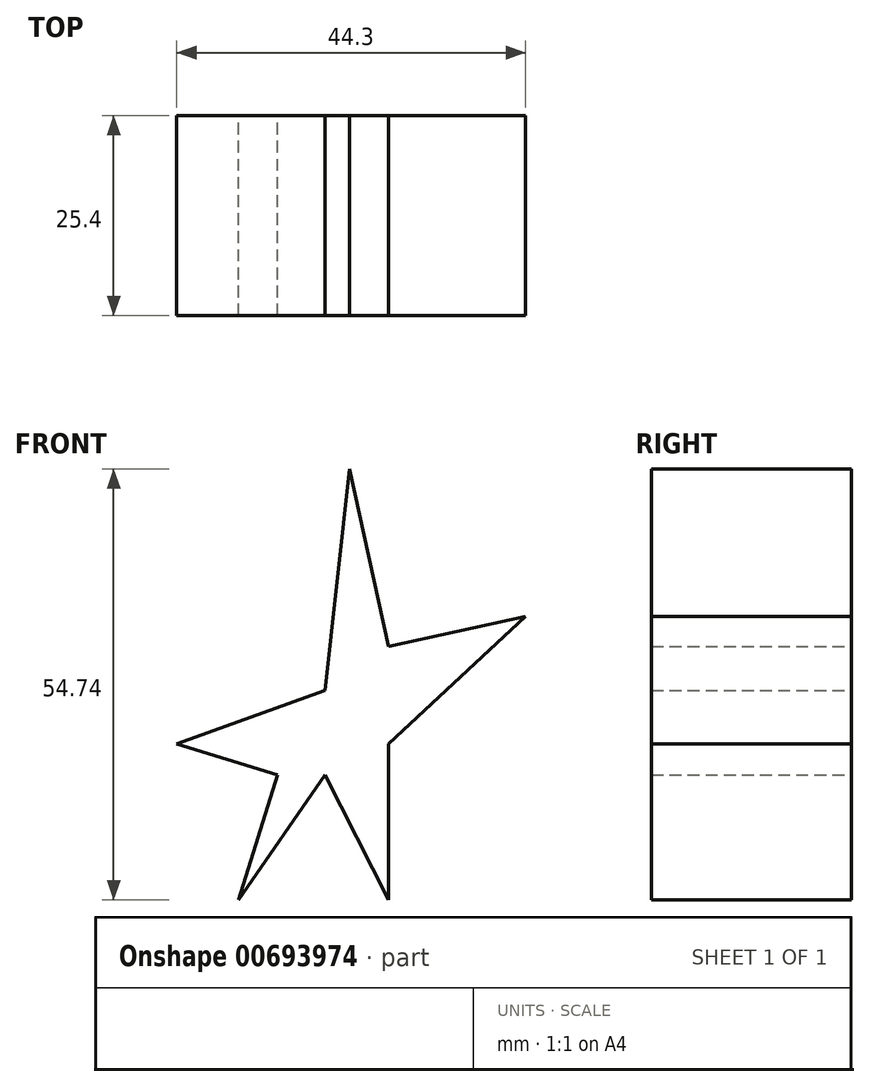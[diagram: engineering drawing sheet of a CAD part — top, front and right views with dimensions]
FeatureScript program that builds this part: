
annotation { "Feature Type Name" : "Feature", "Feature Type Description" : "" }
export const myFeature = defineFeature(function(context is Context, id is Id, definition is map)
    precondition{}
    {
        {
            var Q0;
            Q0=qCreatedBy(makeId("Front.planeOp"),FACE);
            var sketch = newSketch(context, id + "F0", { "sketchPlane" : qUnion([Q0])});
            skLineSegment(sketch, "E0", {"start": v(0, 0) * mm, "end": v(3.11, 28.11) * mm});
            skLineSegment(sketch, "E1", {"start": v(3.11, 28.11) * mm, "end": v(8.03, 5.6) * mm});
            skLineSegment(sketch, "E2", {"start": v(8.03, 5.6) * mm, "end": v(25.46, 9.4) * mm});
            skLineSegment(sketch, "E3", {"start": v(25.46, 9.4) * mm, "end": v(8.03, -6.81) * mm});
            skLineSegment(sketch, "E4", {"start": v(8.03, -6.81) * mm, "end": v(8.03, -26.63) * mm});
            skLineSegment(sketch, "E5", {"start": v(8.03, -26.63) * mm, "end": v(0, -10.77) * mm});
            skLineSegment(sketch, "E6", {"start": v(0, -10.77) * mm, "end": v(-10.98, -26.63) * mm});
            skLineSegment(sketch, "E7", {"start": v(-10.98, -26.63) * mm, "end": v(-6.07, -10.77) * mm});
            skLineSegment(sketch, "E8", {"start": v(-6.07, -10.77) * mm, "end": v(-18.84, -6.81) * mm});
            skLineSegment(sketch, "E9", {"start": v(-18.84, -6.81) * mm, "end": v(0, 0) * mm});
            skSolve(sketch);
        }
        {
            var Q0;
            Q0=makeQuery(id+"F0.imprint","IMPRINT",FACE,{"disambiguationData":[TD([[makeQuery(id+"F0.imprint","IMPRINT",EDGE,{"derivedFrom":sQuery(id+"F0.wireOp",EDGE,"E0")}),-1.0]])]});
            extrude(context, id + "F1", {"entities" : qUnion([Q0]), "depth" : 25.4 * mm, "offsetDistance" : 25.4 * mm});
        }
    });
